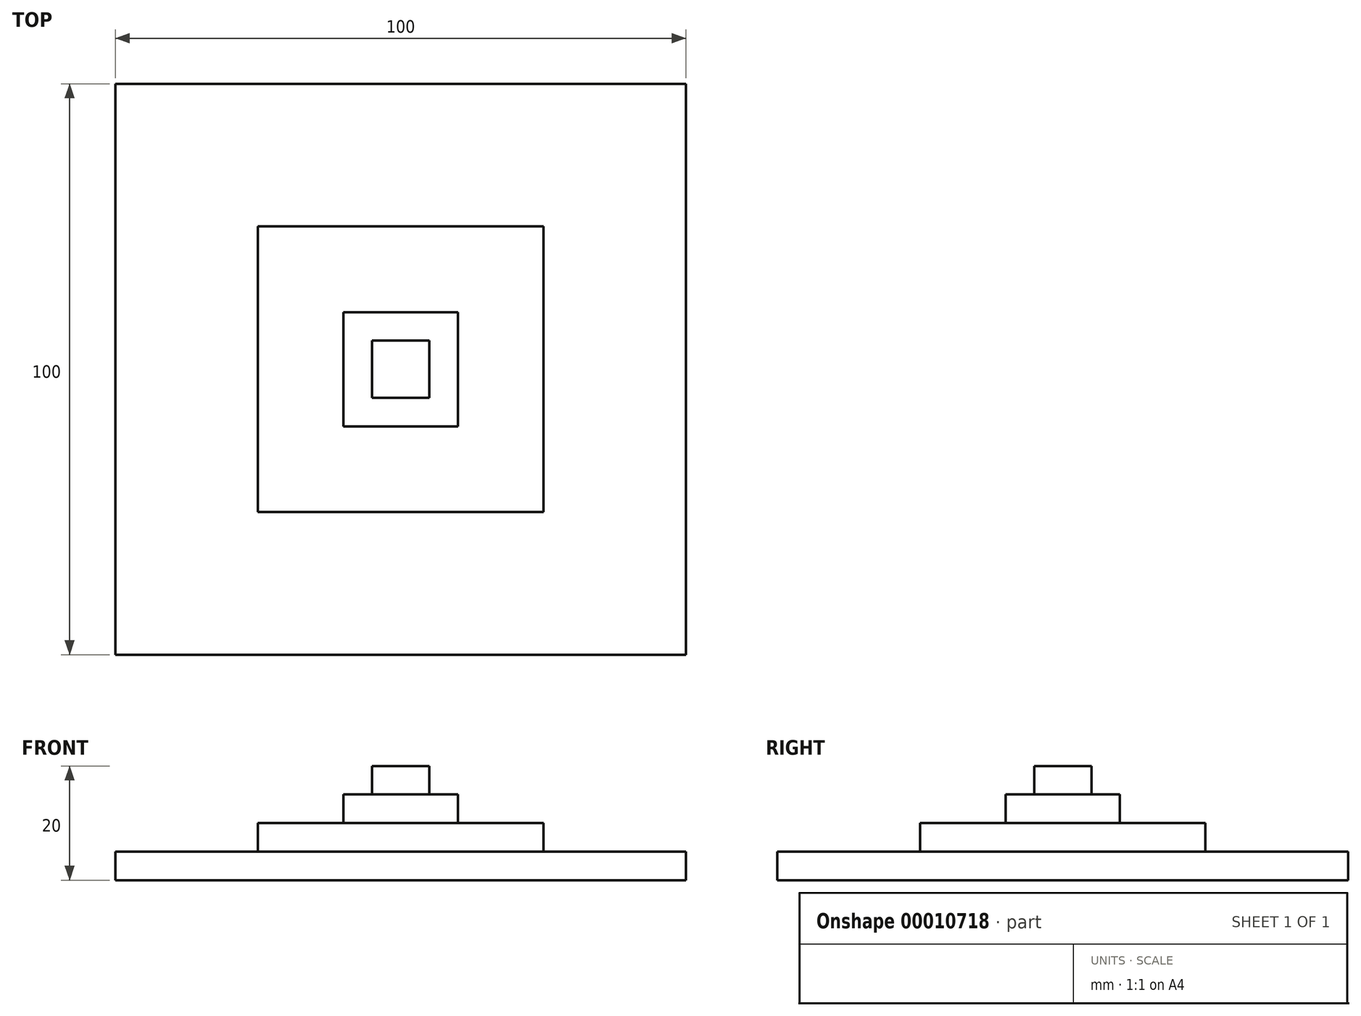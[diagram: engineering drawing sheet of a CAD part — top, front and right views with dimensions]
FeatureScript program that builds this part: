
annotation { "Feature Type Name" : "Feature", "Feature Type Description" : "" }
export const myFeature = defineFeature(function(context is Context, id is Id, definition is map)
    precondition{}
    {
        {
            var Q0;
            Q0=qCreatedBy(makeId("Top.planeOp"),FACE);
            var sketch = newSketch(context, id + "F0", { "sketchPlane" : qUnion([Q0])});
            skLineSegment(sketch, "E0.rect.bottom", {"start": v(50, 50) * mm, "end": v(-50, 50) * mm});
            skLineSegment(sketch, "E0.rect.top", {"start": v(50, -50) * mm, "end": v(-50, -50) * mm});
            skLineSegment(sketch, "E0.rect.left", {"start": v(50, 50) * mm, "end": v(50, -50) * mm});
            skLineSegment(sketch, "E0.rect.right", {"start": v(-50, 50) * mm, "end": v(-50, -50) * mm});
            skPoint(sketch, "E0.rect.middle", {"position": v(0, 0) * mm});
            skSolve(sketch);
        }
        {
            var Q0;
            Q0 = qSketchRegion(id + "F0", true);
            extrude(context, id + "F1", {"entities" : qUnion([Q0]), "depth" : 5 * mm});
        }
        {
            var Q0;
            Q0=makeQuery(id+"F1.opExtrude","CAP_FACE",FACE,{"disambiguationData":[OSD([sQuery(id+"F0.wireOp",EDGE,"E0.rect.bottom"),sQuery(id+"F0.wireOp",EDGE,"E0.rect.top"),sQuery(id+"F0.wireOp",EDGE,"E0.rect.left"),sQuery(id+"F0.wireOp",EDGE,"E0.rect.right")])],"isStart":false});
            var sketch = newSketch(context, id + "F2", { "sketchPlane" : qUnion([Q0])});
            skLineSegment(sketch, "E1.rect.bottom", {"start": v(25, 25) * mm, "end": v(-25, 25) * mm});
            skLineSegment(sketch, "E1.rect.top", {"start": v(25, -25) * mm, "end": v(-25, -25) * mm});
            skLineSegment(sketch, "E1.rect.left", {"start": v(25, 25) * mm, "end": v(25, -25) * mm});
            skLineSegment(sketch, "E1.rect.right", {"start": v(-25, 25) * mm, "end": v(-25, -25) * mm});
            skPoint(sketch, "E1.rect.middle", {"position": v(0, 0) * mm});
            skSolve(sketch);
        }
        {
            var Q0;
            Q0=makeQuery(id+"F2.imprint","IMPRINT",FACE,{"disambiguationData":[TD([[makeQuery(id+"F2.imprint","IMPRINT",EDGE,{"derivedFrom":sQuery(id+"F2.wireOp",EDGE,"E1.rect.bottom")}),1.0]])]});
            extrude(context, id + "F3", {"entities" : qUnion([Q0]), "operationType" : NewBodyOperationType.ADD, "depth" : 5 * mm});
        }
        {
            var Q0;
            Q0=makeQuery(id+"F3.opExtrude","CAP_FACE",FACE,{"disambiguationData":[OSD([sQuery(id+"F2.wireOp",EDGE,"E1.rect.bottom"),sQuery(id+"F2.wireOp",EDGE,"E1.rect.top"),sQuery(id+"F2.wireOp",EDGE,"E1.rect.left"),sQuery(id+"F2.wireOp",EDGE,"E1.rect.right")])],"isStart":false});
            var sketch = newSketch(context, id + "F4", { "sketchPlane" : qUnion([Q0])});
            skLineSegment(sketch, "E2.rect.bottom", {"start": v(10, 10) * mm, "end": v(-10, 10) * mm});
            skLineSegment(sketch, "E2.rect.top", {"start": v(10, -10) * mm, "end": v(-10, -10) * mm});
            skLineSegment(sketch, "E2.rect.left", {"start": v(10, 10) * mm, "end": v(10, -10) * mm});
            skLineSegment(sketch, "E2.rect.right", {"start": v(-10, 10) * mm, "end": v(-10, -10) * mm});
            skPoint(sketch, "E2.rect.middle", {"position": v(0, 0) * mm});
            skSolve(sketch);
        }
        {
            var Q0;
            Q0=makeQuery(id+"F4.imprint","IMPRINT",FACE,{"disambiguationData":[TD([[makeQuery(id+"F4.imprint","IMPRINT",EDGE,{"derivedFrom":sQuery(id+"F4.wireOp",EDGE,"E2.rect.bottom")}),1.0]])]});
            extrude(context, id + "F5", {"entities" : qUnion([Q0]), "operationType" : NewBodyOperationType.ADD, "depth" : 5 * mm});
        }
        {
            var Q0;
            Q0=makeQuery(id+"F5.opExtrude","CAP_FACE",FACE,{"disambiguationData":[OSD([sQuery(id+"F4.wireOp",EDGE,"E2.rect.bottom"),sQuery(id+"F4.wireOp",EDGE,"E2.rect.top"),sQuery(id+"F4.wireOp",EDGE,"E2.rect.left"),sQuery(id+"F4.wireOp",EDGE,"E2.rect.right")])],"isStart":false});
            var sketch = newSketch(context, id + "F6", { "sketchPlane" : qUnion([Q0])});
            skLineSegment(sketch, "E3.rect.bottom", {"start": v(5, 5) * mm, "end": v(-5, 5) * mm});
            skLineSegment(sketch, "E3.rect.top", {"start": v(5, -5) * mm, "end": v(-5, -5) * mm});
            skLineSegment(sketch, "E3.rect.left", {"start": v(5, 5) * mm, "end": v(5, -5) * mm});
            skLineSegment(sketch, "E3.rect.right", {"start": v(-5, 5) * mm, "end": v(-5, -5) * mm});
            skPoint(sketch, "E3.rect.middle", {"position": v(0, 0) * mm});
            skSolve(sketch);
        }
        {
            var Q0;
            Q0=makeQuery(id+"F6.imprint","IMPRINT",FACE,{"disambiguationData":[TD([[makeQuery(id+"F6.imprint","IMPRINT",EDGE,{"derivedFrom":sQuery(id+"F6.wireOp",EDGE,"E3.rect.bottom")}),1.0]])]});
            extrude(context, id + "F7", {"entities" : qUnion([Q0]), "operationType" : NewBodyOperationType.ADD, "depth" : 5 * mm});
        }
    });
